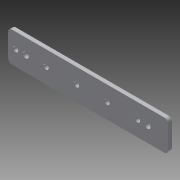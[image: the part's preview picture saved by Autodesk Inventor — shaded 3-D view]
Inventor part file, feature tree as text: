
AUTODESK INVENTOR PART (.ipt)
format: ipt  version: 2014 (Build 180170000, 170)  size: 99,328 bytes
history: native  units: in
note: dims shown in document units (in); Inventor stores cm internally (conversion verified against a paired STEP export)
features: extrude x1, fillet x1, sketch x1
ambient origin geometry x8: Origin, YZ Plane, XZ Plane, XY Plane, X Axis, Y Axis, Z Axis, Center Point
bodies: Solid1 (feature_tree)
feature tree (3):
  extrude  "Extrusion1"  Depth=1.0in
  fillet  "Fillet1"  Radius=0.163in
  sketch  "Sketch1"  dims[d0=5.25in d1=1.0in d2=0.163in d3=0.5in d4=0.25in d5=1.9685in d7=1.0in d8=0.3937in d10=1.0in d12=0.19in d13=0.7874in d15=4.0in d16=0.3937in d18=1.0in d21=0.33in d22=0.5in d23=0.125in d24=0.0in d25=0.125in]
